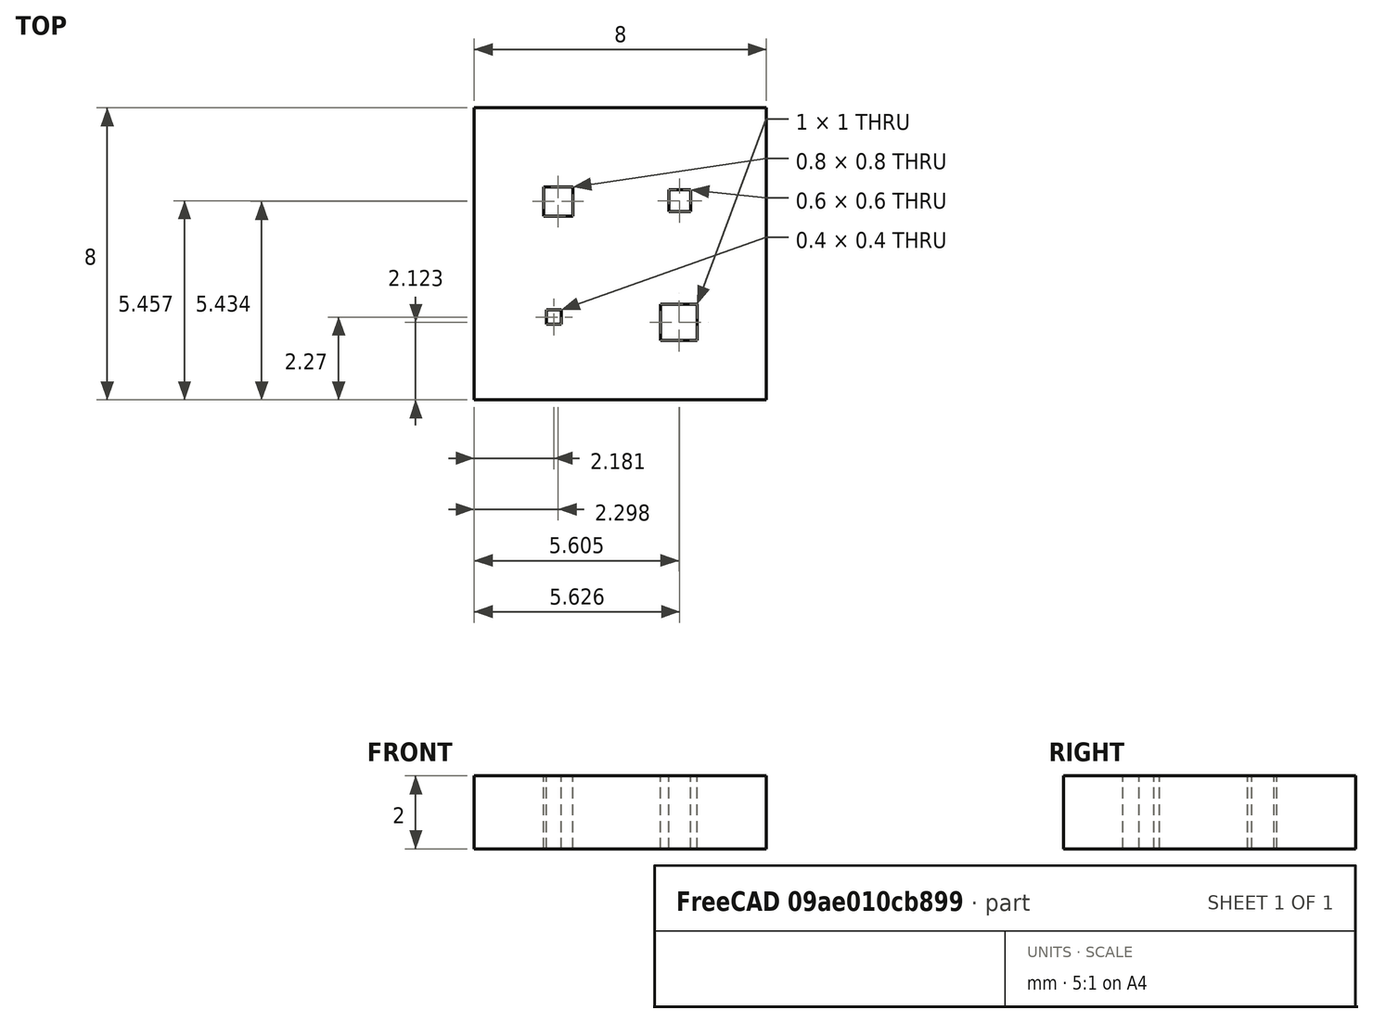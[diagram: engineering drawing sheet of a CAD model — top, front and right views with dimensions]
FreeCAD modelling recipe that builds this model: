
FCSTD DOCUMENT  (FreeCAD 0.17R13519 (Git))
Label: gt1
License: All rights reserved
LicenseURL: http://en.wikipedia.org/wiki/All_rights_reserved
objects: Sketcher::SketchObject×1, PartDesign::Pad×1, PartDesign::Body×1
note: 4 computed .brp shape members not serialized (recipe doc carries the construction recipe); baked Part::Feature solids carry a one-line shape summary decoded from their .brp

FEATURE [Sketcher::SketchObject] Sketch
  MapMode = 5
  Support = -> [XY_Plane]
  sketch-geometry (20):
    g0: LineSegment StartX=0 StartY=0 StartZ=0 EndX=8 EndY=0 EndZ=0
    g1: LineSegment StartX=8 StartY=0 StartZ=0 EndX=8 EndY=8 EndZ=0
    g2: LineSegment StartX=8 StartY=8 StartZ=0 EndX=0 EndY=8 EndZ=0
    g3: LineSegment StartX=0 StartY=8 StartZ=0 EndX=0 EndY=0 EndZ=0
    g4: LineSegment StartX=1.98087 StartY=2.46956 StartZ=0 EndX=2.38087 EndY=2.46956 EndZ=0
    g5: LineSegment StartX=2.38087 StartY=2.46956 StartZ=0 EndX=2.38087 EndY=2.06956 EndZ=0
    g6: LineSegment StartX=2.38087 StartY=2.06956 StartZ=0 EndX=1.98087 EndY=2.06956 EndZ=0
    g7: LineSegment StartX=1.98087 StartY=2.06956 StartZ=0 EndX=1.98087 EndY=2.46956 EndZ=0
    g8: LineSegment StartX=5.92591 StartY=5.75654 StartZ=0 EndX=5.32591 EndY=5.75654 EndZ=0
    g9: LineSegment StartX=5.32591 StartY=5.75654 StartZ=0 EndX=5.32591 EndY=5.15654 EndZ=0
    g10: LineSegment StartX=5.32591 StartY=5.15654 StartZ=0 EndX=5.92591 EndY=5.15654 EndZ=0
    g11: LineSegment StartX=5.92591 StartY=5.15654 StartZ=0 EndX=5.92591 EndY=5.75654 EndZ=0
    g12: LineSegment StartX=1.89796 StartY=5.83359 StartZ=0 EndX=2.69796 EndY=5.83359 EndZ=0
    g13: LineSegment StartX=2.69796 StartY=5.83359 StartZ=0 EndX=2.69796 EndY=5.03359 EndZ=0
    g14: LineSegment StartX=2.69796 StartY=5.03359 StartZ=0 EndX=1.89796 EndY=5.03359 EndZ=0
    g15: LineSegment StartX=1.89796 StartY=5.03359 StartZ=0 EndX=1.89796 EndY=5.83359 EndZ=0
    g16: LineSegment StartX=5.10472 StartY=2.62332 StartZ=0 EndX=6.10472 EndY=2.62332 EndZ=0
    g17: LineSegment StartX=6.10472 StartY=2.62332 StartZ=0 EndX=6.10472 EndY=1.62332 EndZ=0
    g18: LineSegment StartX=6.10472 StartY=1.62332 StartZ=0 EndX=5.10472 EndY=1.62332 EndZ=0
    g19: LineSegment StartX=5.10472 StartY=1.62332 StartZ=0 EndX=5.10472 EndY=2.62332 EndZ=0
  constraints (51):
    c: Coincident(g0,g1)
    c: Coincident(g1,g2)
    c: Coincident(g2,g3)
    c: Coincident(g3,g0)
    c: Horizontal(g0)
    c: Horizontal(g2)
    c: Vertical(g1)
    c: Vertical(g3)
    c: Coincident(g0,g-1)
    c: Distance(g0) = 8
    c: Distance(g3) = 8
    c: Coincident(g4,g5)
    c: Coincident(g5,g6)
    c: Coincident(g6,g7)
    c: Coincident(g7,g4)
    c: Horizontal(g4)
    c: Horizontal(g6)
    c: Vertical(g5)
    c: Vertical(g7)
    c: Distance(g7) = 0.4
    c: Distance(g6) = 0.4
    c: Coincident(g8,g9)
    c: Coincident(g9,g10)
    c: Coincident(g10,g11)
    c: Coincident(g11,g8)
    c: Horizontal(g8)
    c: Horizontal(g10)
    c: Vertical(g9)
    c: Vertical(g11)
    c: Distance(g10) = 0.6
    c: Distance(g9) = 0.6
    c: Coincident(g12,g13)
    c: Coincident(g13,g14)
    c: Coincident(g14,g15)
    c: Coincident(g15,g12)
    c: Horizontal(g12)
    c: Horizontal(g14)
    c: Vertical(g13)
    c: Vertical(g15)
    c: Equal(g14,g15)
    c: Coincident(g16,g17)
    c: Coincident(g17,g18)
    c: Coincident(g18,g19)
    c: Coincident(g19,g16)
    c: Horizontal(g16)
    c: Horizontal(g18)
    c: Vertical(g17)
    c: Vertical(g19)
    c: Equal(g18,g19)
    c: Distance(g15) = 0.8
    c: Distance(g19) = 1
FEATURE [PartDesign::Pad] Pad
  Length = 2
  Length2 = 100
  Profile = -> Sketch
  Type = 0
FEATURE [PartDesign::Body] Body
  Group = -> [Sketch,Pad]
  Origin = -> Origin
  Tip = -> Pad
